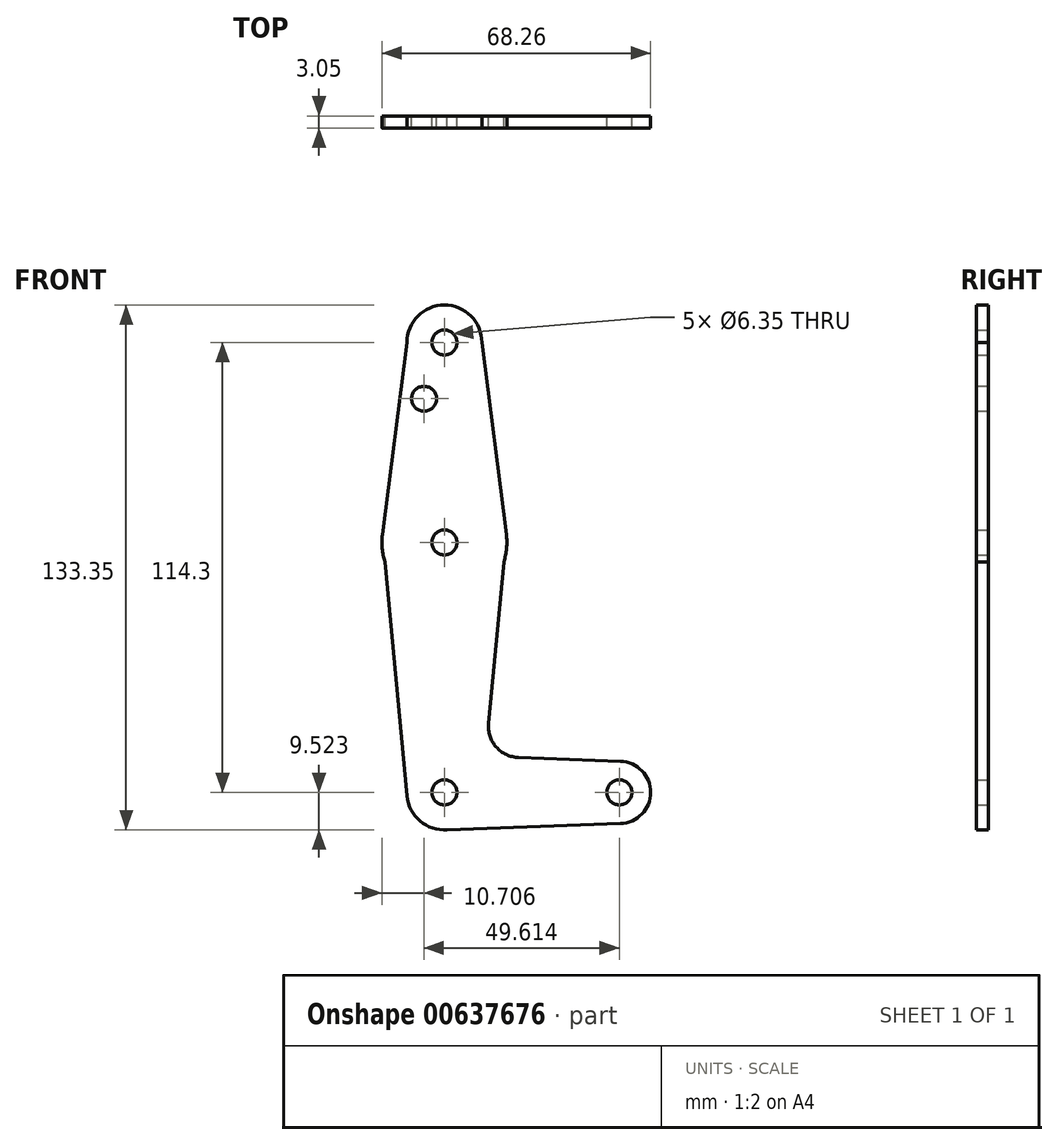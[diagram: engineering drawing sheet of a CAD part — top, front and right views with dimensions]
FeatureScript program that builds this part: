
annotation { "Feature Type Name" : "Feature", "Feature Type Description" : "" }
export const myFeature = defineFeature(function(context is Context, id is Id, definition is map)
    precondition{}
    {
        {
            var Q0;
            Q0=qCreatedBy(makeId("Front.planeOp"),FACE);
            var sketch = newSketch(context, id + "F0", { "sketchPlane" : qUnion([Q0])});
            skLineSegment(sketch, "E0", {"start": v(0, 114.17) * mm, "end": v(0, -0.13) * mm, "construction": true});
            skLineSegment(sketch, "E1", {"start": v(0, -0.13) * mm, "end": v(44.45, -0.13) * mm});
            skCircle(sketch, "E2", {"center": v(0, 114.17) * mm, "radius": 9.53 * mm});
            skCircle(sketch, "E3", {"center": v(0, 63.37) * mm, "radius": 15.88 * mm});
            skCircle(sketch, "E4", {"center": v(0, -0.13) * mm, "radius": 9.53 * mm});
            skCircle(sketch, "E5", {"center": v(44.45, -0.13) * mm, "radius": 7.94 * mm});
            skLineSegment(sketch, "E6", {"start": v(-9.52, 114.17) * mm, "end": v(-15.75, 65.38) * mm});
            skLineSegment(sketch, "E7", {"start": v(9.52, 114.17) * mm, "end": v(15.75, 65.38) * mm});
            skLineSegment(sketch, "E8", {"start": v(-15.75, 65.38) * mm, "end": v(-9.48, -1.02) * mm});
            skLineSegment(sketch, "E9", {"start": v(15.75, 65.38) * mm, "end": v(11.22, 17.42) * mm});
            skLineSegment(sketch, "E10", {"start": v(0, -9.65) * mm, "end": v(44.73, -8.06) * mm});
            skLineSegment(sketch, "E11", {"start": v(18.85, 8.73) * mm, "end": v(44.73, 7.8) * mm});
            skCircle(sketch, "E12", {"center": v(-5.16, 99.9) * mm, "radius": 3.18 * mm});
            skCircle(sketch, "E13", {"center": v(0, 63.37) * mm, "radius": 3.18 * mm});
            skCircle(sketch, "E14", {"center": v(0, -0.13) * mm, "radius": 3.18 * mm});
            skCircle(sketch, "E15", {"center": v(44.45, -0.13) * mm, "radius": 3.18 * mm});
            skCircle(sketch, "E16", {"center": v(0, 114.17) * mm, "radius": 3.18 * mm});
            skPoint(sketch, "E17.newPointA", {"position": v(0, 9.4) * mm});
            skArc(sketch, "E17.filletArc", {"start": v(11.22, 17.42) * mm, "mid": v(13.16, 11.43) * mm, "end": v(18.85, 8.73) * mm});
            skSolve(sketch);
        }
        {
            var Q0;
            Q0 = qSketchRegion(id + "F0", true);
            extrude(context, id + "F1", {"entities" : qUnion([Q0]), "depth" : 3.05 * mm, "offsetDistance" : 25.4 * mm});
        }
    });
